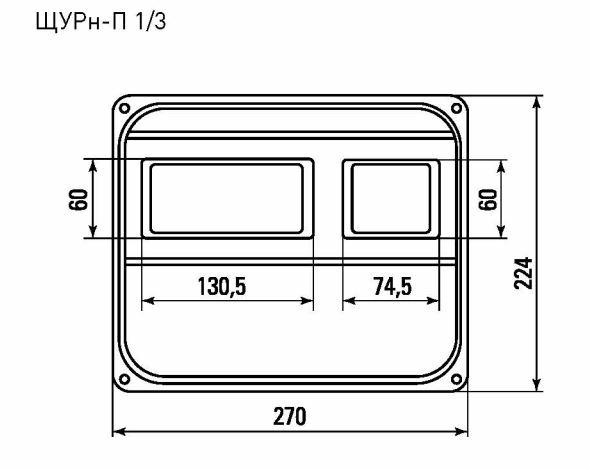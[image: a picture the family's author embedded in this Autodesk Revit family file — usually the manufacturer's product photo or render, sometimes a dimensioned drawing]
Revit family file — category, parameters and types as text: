
# Revit family: EKF_EE_Короб_Универсальный_С_Компенсатором(670х300х160)_Basic
name_source: partatom
category: Электрооборудование
units: mm (PartAtom-declared; Revit-internal decimal feet)

## family parameters
Всегда вертикально = Да
На основе рабочей плоскости = Нет
Общий = Нет
При загрузке вырезать с полостями = Нет
Размер круглого соединителя = Использовать диаметр
Тип детали = Силовой щит
Точка расчета площади = Да

## types (1)
- Короб универсальный с компенсатором (670х300х160) EKF Basic
    ADSK_Единица измерения = компл.
    ADSK_Завод-изготовитель = EKF
    ADSK_Классификация нагрузок = Прочее
    ADSK_Код изделия = uerms-01kor
    ADSK_Количество = 1
    ADSK_Количество фаз = 3
    ADSK_Коэффициент мощности = 1
    ADSK_Марка = Короб универсальный с компенсатором
    ADSK_Масса = 0
    ADSK_Материал = RAL 7035_Сталь
    ADSK_Наименование = Короб универсальный с компенсатором (670х300х160) EKF BasicКороб универсальный с компенсатором (670х300х160) EKF Basic
    ADSK_Напряжение = 400 В
    ADSK_Номинальная мощность = 0 Вт
    ADSK_Обозначение = Короб универсальный с компенсатором
    ADSK_Полная мощность = 0 В·А
    ADSK_Размер_Высота = 670 мм
    ADSK_Размер_Глубина = 160 мм
    ADSK_Размер_Ширина = 300 мм
    ADSK_Ток = 125 А
    Изготовитель = EKF
    Количество DIN-реек = 0
    Количество модулей на DIN-рейке = 0
    Максимальное количество модулей = 0
    Описание = Короб универсальный с компенсатором (670х300х160) EKF BasicКороб универсальный с компенсатором (670х300х160) EKF Basic
    Серия номенклатуры = Basic
    Степень защиты IP = IP31
    ТВ = EKF
    Тип = 219 мм
    Тип установки = Навесной
